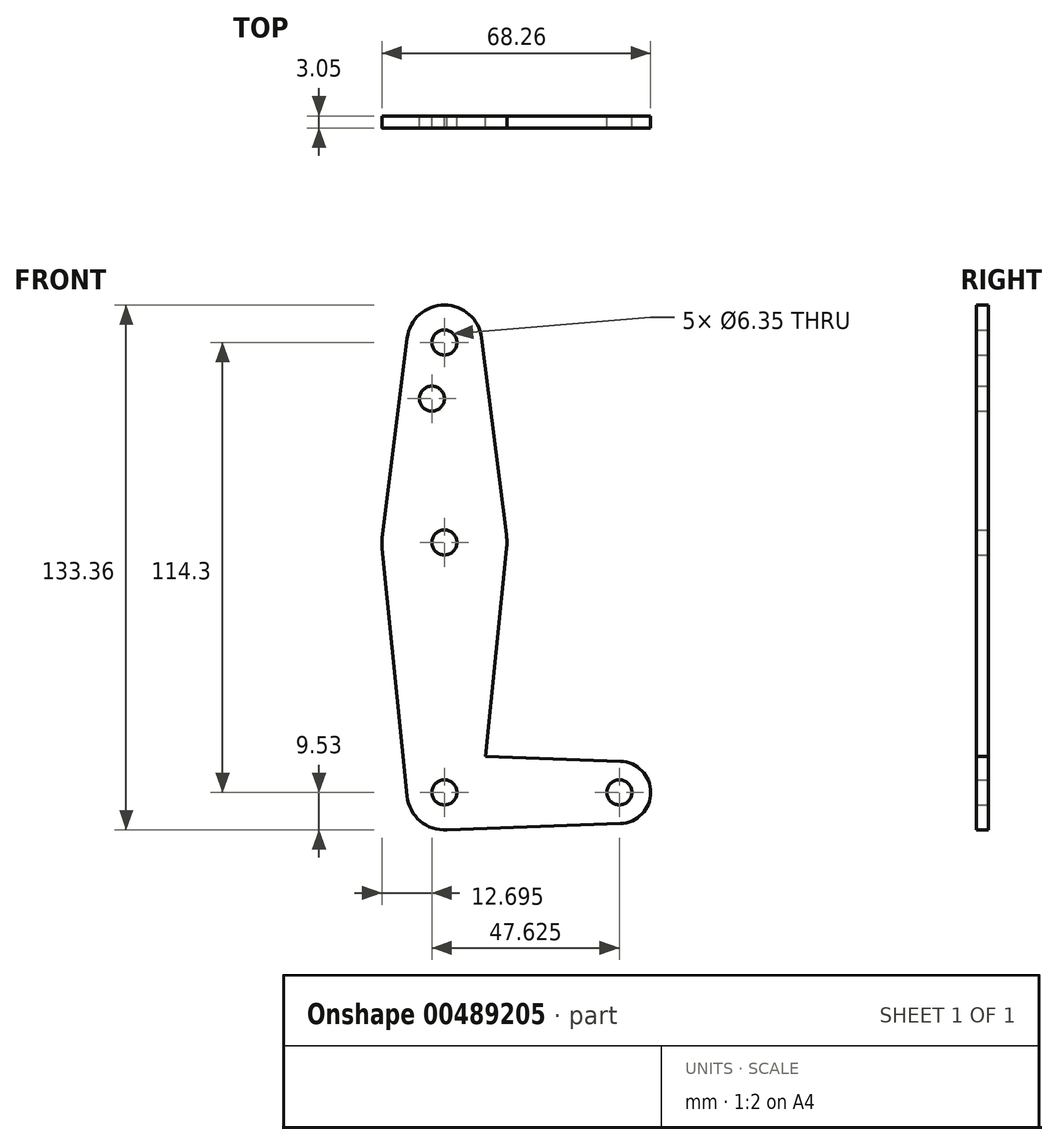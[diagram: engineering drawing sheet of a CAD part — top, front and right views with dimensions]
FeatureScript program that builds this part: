
annotation { "Feature Type Name" : "Feature", "Feature Type Description" : "" }
export const myFeature = defineFeature(function(context is Context, id is Id, definition is map)
    precondition{}
    {
        {
            var Q0;
            Q0=qCreatedBy(makeId("Front.planeOp"),FACE);
            var sketch = newSketch(context, id + "F0", { "sketchPlane" : qUnion([Q0])});
            skLineSegment(sketch, "E0", {"start": v(0, 0) * mm, "end": v(0, 114.3) * mm, "construction": true});
            skLineSegment(sketch, "E1", {"start": v(0, 0) * mm, "end": v(44.45, 0) * mm, "construction": true});
            skCircle(sketch, "E2", {"center": v(44.45, 0) * mm, "radius": 7.94 * mm});
            skCircle(sketch, "E3", {"center": v(0, 0) * mm, "radius": 9.53 * mm});
            skCircle(sketch, "E4", {"center": v(0, 63.5) * mm, "radius": 15.88 * mm});
            skCircle(sketch, "E5", {"center": v(0, 114.3) * mm, "radius": 9.53 * mm});
            skLineSegment(sketch, "E6", {"start": v(0, 0) * mm, "end": v(0, 63.5) * mm, "construction": true});
            skLineSegment(sketch, "E7", {"start": v(-9.45, 115.5) * mm, "end": v(-15.75, 65.48) * mm});
            skLineSegment(sketch, "E8", {"start": v(0, -9.52) * mm, "end": v(44.73, -7.93) * mm});
            skLineSegment(sketch, "E9", {"start": v(44.73, 7.93) * mm, "end": v(0, 9.53) * mm});
            skLineSegment(sketch, "E10", {"start": v(9.45, 115.5) * mm, "end": v(15.75, 65.48) * mm});
            skCircle(sketch, "E11", {"center": v(44.45, 0) * mm, "radius": 3.18 * mm});
            skCircle(sketch, "E12", {"center": v(0, 0) * mm, "radius": 3.18 * mm});
            skCircle(sketch, "E13", {"center": v(0, 63.5) * mm, "radius": 3.18 * mm});
            skLineSegment(sketch, "E14", {"start": v(0, 63.5) * mm, "end": v(0, 100.03) * mm});
            skCircle(sketch, "E15", {"center": v(0, 114.3) * mm, "radius": 3.18 * mm});
            skLineSegment(sketch, "E16", {"start": v(-3.17, 100.03) * mm, "end": v(0, 100.03) * mm});
            skCircle(sketch, "E17", {"center": v(-3.17, 100.03) * mm, "radius": 3.18 * mm});
            skPoint(sketch, "E18.end.orphan", {"position": v(-9.57, 0) * mm});
            skLineSegment(sketch, "E19", {"start": v(-15.8, 61.91) * mm, "end": v(-9.48, -0.95) * mm});
            skLineSegment(sketch, "E20", {"start": v(9.48, -0.95) * mm, "end": v(15.8, 61.91) * mm});
            skSolve(sketch);
        }
        {
            var Q0;
            Q0 = qSketchRegion(id + "F0", true);
            extrude(context, id + "F1", {"entities" : qUnion([Q0]), "depth" : 3.05 * mm});
        }
    });
